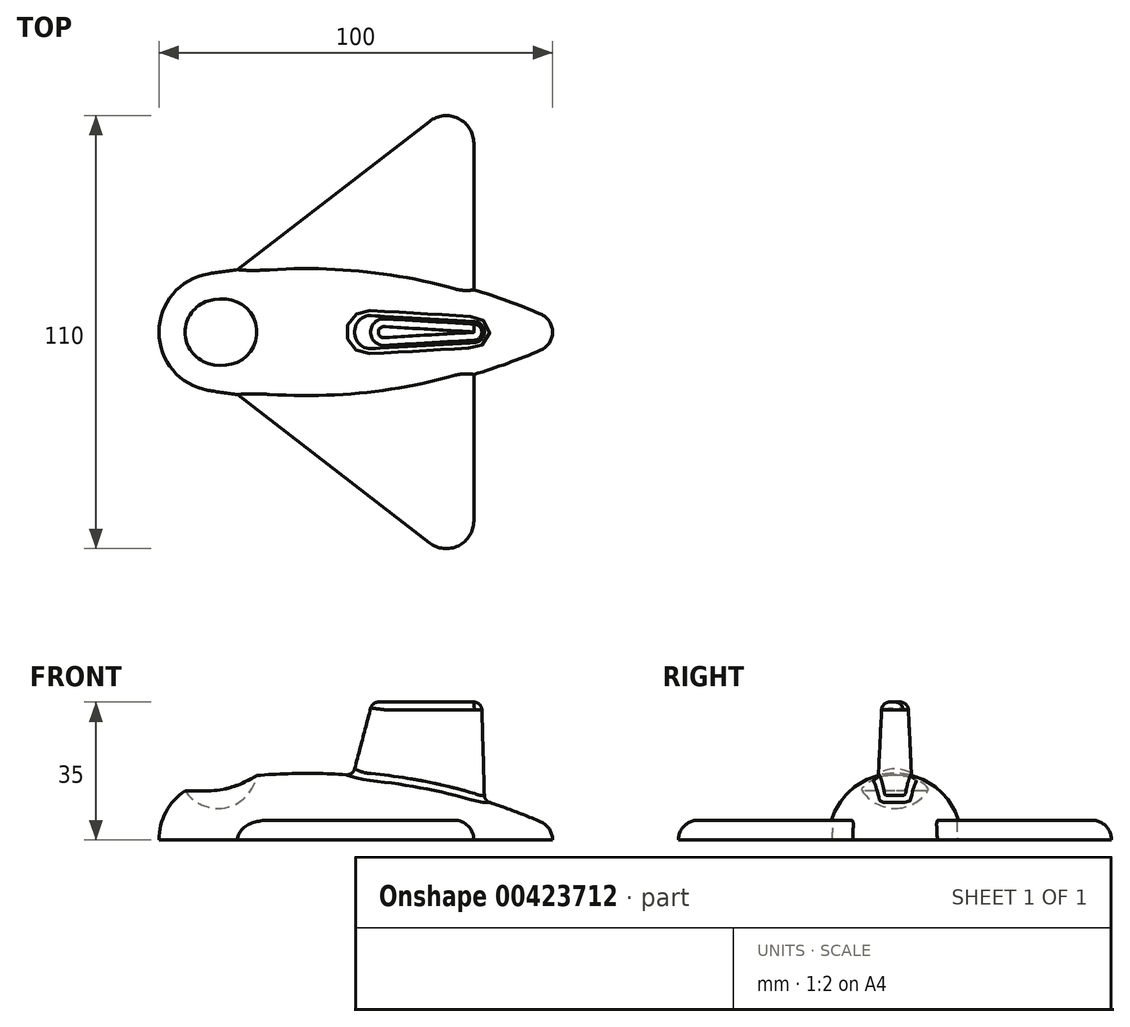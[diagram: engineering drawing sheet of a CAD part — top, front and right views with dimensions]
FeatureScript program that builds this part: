
annotation { "Feature Type Name" : "Feature", "Feature Type Description" : "" }
export const myFeature = defineFeature(function(context is Context, id is Id, definition is map)
    precondition{}
    {
        {
            var Q0;
            Q0=qCreatedBy(makeId("Top.planeOp"),FACE);
            var sketch = newSketch(context, id + "F0", { "sketchPlane" : qUnion([Q0])});
            skArc(sketch, "E0", {"start": v(-2.5, 14.8) * mm, "mid": v(-11.46, 9.68) * mm, "end": v(-15, 0) * mm});
            skArc(sketch, "E1", {"start": v(85, 0) * mm, "mid": v(84.18, 2.75) * mm, "end": v(81.98, 4.6) * mm});
            skArc(sketch, "E2", {"start": v(81.98, 4.6) * mm, "mid": v(40.48, 15.8) * mm, "end": v(-2.5, 14.8) * mm});
            skLineSegment(sketch, "E3", {"start": v(-21.3, 0) * mm, "end": v(161.85, 0) * mm, "construction": true});
            skLineSegment(sketch, "E4", {"start": v(-15, 0) * mm, "end": v(85, 0) * mm});
            skSolve(sketch);
        }
        {
            var Q0;
            Q0=makeQuery(id+"F0.imprint","IMPRINT",FACE,{"disambiguationData":[TD([[makeQuery(id+"F0.imprint","IMPRINT",EDGE,{"derivedFrom":sQuery(id+"F0.wireOp",EDGE,"E0")}),1.0]])]});
            var Q1;
            Q1=sQuery(id+"F0.wireOp",EDGE,"E3");
            revolve(context, id + "F1", {"entities" : qUnion([Q0]), "axis" : qUnion([Q1]), "revolveType" : RevolveType.ONE_DIRECTION, "angle" : 180 * degree});
        }
        {
            var Q0;
            Q0=qCreatedBy(makeId("Front.planeOp"),FACE);
            var sketch = newSketch(context, id + "F2", { "sketchPlane" : qUnion([Q0])});
            skArc(sketch, "E5", {"start": v(0, 8) * mm, "mid": v(10, 18) * mm, "end": v(0, 28) * mm});
            skLineSegment(sketch, "E6", {"start": v(0, 28) * mm, "end": v(0, 8) * mm});
            skSolve(sketch);
        }
        {
            var Q0;
            Q0=makeQuery(id+"F2.imprint","IMPRINT",FACE,{"disambiguationData":[TD([[makeQuery(id+"F2.imprint","IMPRINT",EDGE,{"derivedFrom":sQuery(id+"F2.wireOp",EDGE,"E5")}),1.0]])]});
            var Q1;
            Q1=sQuery(id+"F2.wireOp",EDGE,"E6");
            revolve(context, id + "F3", {"operationType" : NewBodyOperationType.REMOVE, "entities" : qUnion([Q0]), "axis" : qUnion([Q1]), "revolveType" : RevolveType.FULL, "oppositeDirection" : true});
        }
        {
            var Q0;
            Q0=qCreatedBy(makeId("Top.planeOp"),FACE);
            cPlane(context, id + "F4", {"entities" : qUnion([Q0]), "cplaneType" : CPlaneType.OFFSET, "offset" : 35 * mm, "width" : 150 * mm, "height" : 150 * mm});
        }
        {
            var Q0;
            Q0=qCreatedBy(id+"F4.planeOp",FACE);
            var sketch = newSketch(context, id + "F5", { "sketchPlane" : qUnion([Q0])});
            skArc(sketch, "E7", {"start": v(42.7, 3.3) * mm, "mid": v(39.2, 0) * mm, "end": v(42.7, -3.3) * mm});
            skArc(sketch, "E8", {"start": v(65.12, -2) * mm, "mid": v(67, 0) * mm, "end": v(65.12, 2) * mm});
            skLineSegment(sketch, "E9", {"start": v(42.7, 3.3) * mm, "end": v(65.12, 2) * mm});
            skLineSegment(sketch, "E10", {"start": v(42.7, -3.3) * mm, "end": v(65.12, -2) * mm});
            skSolve(sketch);
        }
        {
            var Q0;
            Q0=qCreatedBy(makeId("Top.planeOp"),FACE);
            var sketch = newSketch(context, id + "F6", { "sketchPlane" : qUnion([Q0])});
            skPoint(sketch, "E11.0", {"position": v(65, 0) * mm});
            skArc(sketch, "E12", {"start": v(65.2, -3) * mm, "mid": v(68, 0) * mm, "end": v(65.2, 3) * mm});
            skArc(sketch, "E13", {"start": v(35.33, 4.99) * mm, "mid": v(30, 0) * mm, "end": v(35.33, -4.99) * mm});
            skLineSegment(sketch, "E14", {"start": v(35.33, 4.99) * mm, "end": v(65.2, 3) * mm});
            skLineSegment(sketch, "E15", {"start": v(35.33, -4.99) * mm, "end": v(65.2, -3) * mm});
            skSolve(sketch);
        }
        {
            var Q1;
            Q1=makeQuery(id+"F5.imprint","IMPRINT",FACE,{"disambiguationData":[TD([[makeQuery(id+"F5.imprint","IMPRINT",EDGE,{"derivedFrom":sQuery(id+"F5.wireOp",EDGE,"E7")}),1.0]])]});
            var Q2;
            Q2 = qSketchRegion(id + "F6", true);
            loft(context, id + "F7", {"operationType" : NewBodyOperationType.ADD, "sheetProfilesArray" : [{ "sheetProfileEntities" : qUnion([Q1]) }, { "sheetProfileEntities" : qUnion([Q2]) }]});
        }
        {
            var Q0;
            Q0=qCreatedBy(makeId("Top.planeOp"),FACE);
            var sketch = newSketch(context, id + "F8", { "sketchPlane" : qUnion([Q0])});
            skLineSegment(sketch, "E16", {"start": v(53.72, 53.54) * mm, "end": v(-2.69, 9.92) * mm});
            skLineSegment(sketch, "E17", {"start": v(65, 48) * mm, "end": v(65, 6.87) * mm});
            skLineSegment(sketch, "E18", {"start": v(65, 6.87) * mm, "end": v(-2.69, 9.92) * mm});
            skArc(sketch, "E19.0", {"start": v(81.98, 4.6) * mm, "mid": v(40.48, 15.8) * mm, "end": v(-2.5, 14.8) * mm, "construction": true});
            skPoint(sketch, "E20", {"position": v(5, 15.86) * mm});
            skPoint(sketch, "E21.visualSharp", {"position": v(65, 62.26) * mm});
            skArc(sketch, "E21.filletArc", {"start": v(65, 48) * mm, "mid": v(61.08, 54.28) * mm, "end": v(53.72, 53.54) * mm});
            skLineSegment(sketch, "E22", {"start": v(34.8, 55) * mm, "end": v(127.28, 55) * mm, "construction": true});
            skLineSegment(sketch, "E23.MirrorCS", {"start": v(65, -48) * mm, "end": v(65, -6.87) * mm});
            skArc(sketch, "E24.MirrorCS", {"start": v(65, -48) * mm, "mid": v(61.08, -54.28) * mm, "end": v(53.72, -53.54) * mm});
            skLineSegment(sketch, "E25.MirrorCS", {"start": v(53.72, -53.54) * mm, "end": v(-2.69, -9.92) * mm});
            skLineSegment(sketch, "E26.MirrorCS", {"start": v(65, -6.87) * mm, "end": v(-2.69, -9.92) * mm});
            skSolve(sketch);
        }
        {
            var Q0;
            Q0 = qSketchRegion(id + "F8", true);
            extrude(context, id + "F9", {"entities" : qUnion([Q0]), "operationType" : NewBodyOperationType.ADD, "depth" : 5 * mm});
        }
        {
            var Q0;
            Q0=makeQuery(id+"F9.opExtrude","CAP_EDGE",EDGE,{"disambiguationData":[OSD([sQuery(id+"F8.wireOp",EDGE,"E21.filletArc")])],"isStart":false});
            var Q1;
            Q1=makeQuery(id+"F9.opExtrude","CAP_EDGE",EDGE,{"disambiguationData":[OSD([sQuery(id+"F8.wireOp",EDGE,"E23.MirrorCS")])],"isStart":false});
            fillet(context, id + "F10", {"entities" : qUnion([Q0, Q1]), "radius" : 5 * mm, "tangentPropagation" : true, "allowEdgeOverflow" : false});
        }
        {
            var Q0;
            Q0=makeQuery(id+"F7.opLoft","MID_CAP_EDGE",EDGE,{"disambiguationData":[OSD([sQuery(id+"F5.wireOp",EDGE,"E7"),sQuery(id+"F5.wireOp",EDGE,"E8"),sQuery(id+"F5.wireOp",EDGE,"E10")])],"capPos":0.0});
            fillet(context, id + "F11", {"entities" : qUnion([Q0]), "radius" : 2 * mm, "tangentPropagation" : true, "allowEdgeOverflow" : false});
        }
        {
            var Q0;
            Q0=makeQuery(id+"F7.boolean.opBoolean","INTERSECT",EDGE,{"derivedFrom":[makeQuery(id+"F1.opRevolve","SWEPT_FACE",FACE,{"disambiguationData":[OSD([sQuery(id+"F0.wireOp",EDGE,"E2")])]}),makeQuery(id+"F7.opLoft","SWEPT_FACE",FACE,{"disambiguationData":[OSD([sQuery(id+"F5.wireOp",EDGE,"E7"),sQuery(id+"F5.wireOp",EDGE,"E8"),sQuery(id+"F5.wireOp",EDGE,"E9"),sQuery(id+"F6.wireOp",EDGE,"E12"),sQuery(id+"F6.wireOp",EDGE,"E13"),sQuery(id+"F6.wireOp",EDGE,"E14")])]})]});
            fillet(context, id + "F12", {"entities" : qUnion([Q0]), "radius" : 2 * mm, "tangentPropagation" : true, "allowEdgeOverflow" : false});
        }
    });
